# Revit family: Storage-Teknion-PLDBS_Bar_Height_Drawer_Cabinet_Standard-R2015
name_source: partatom
category: Furniture
revit_build: Autodesk Revit Architecture 2015 (Build: 20140323_1530(x64)
units: mm (PartAtom-declared; Revit-internal decimal feet)

## types (1)
- Bar Height Drawer Cabinet - Standard
    Assembly Code = E2020200
    Available Drawer Combination = [checked]= File/File/Extra Large File [unchecked]= Large File/Large File/ File
    Description = Bar Height Drawer Cabinet - 40" High
    Height = 40 "
    Manufacturer = Teknion
    Manufacturer Fax = 416.661.4586
    Model = PLDBS_
    Part Number = PLDBS
    Product Documentation Link = http://www.teknion.com
    Product Line = Filing and Storage
    Product Page URL = http://www.teknion.com
    Series = Ledger Plus
    Sustainability Data = http://www.teknion.com
    URL = www.teknion.com
    Unit Weight URL = http://www.teknion.com
    Warranty = http://www.teknion.com

## geometry (parser evidence)
native form markers: Sweep x2
no freeform markers — native parametric forms only
